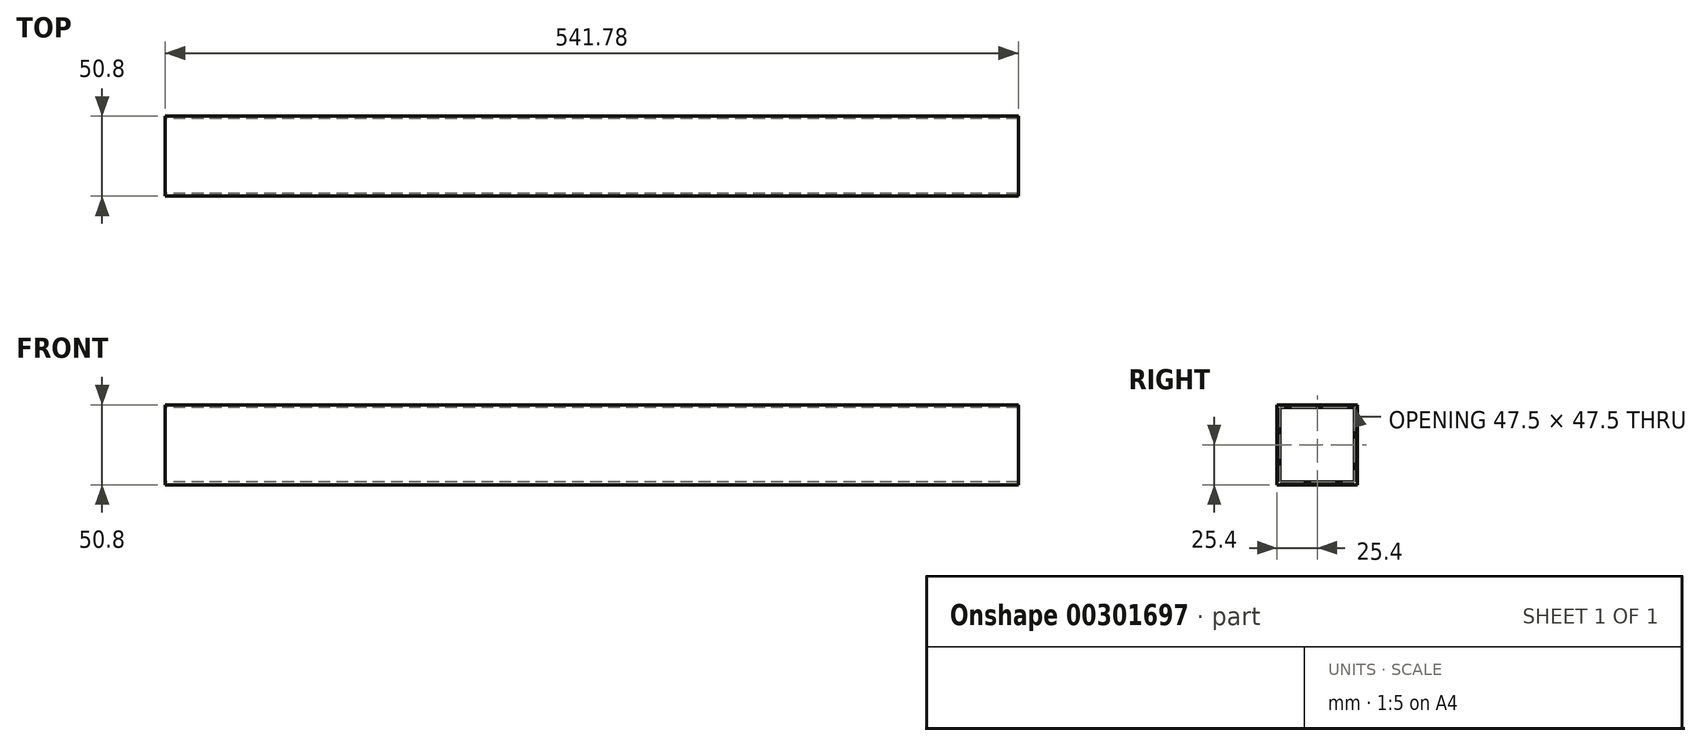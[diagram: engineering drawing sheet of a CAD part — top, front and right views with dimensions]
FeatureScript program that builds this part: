
annotation { "Feature Type Name" : "Feature", "Feature Type Description" : "" }
export const myFeature = defineFeature(function(context is Context, id is Id, definition is map)
    precondition{}
    {
        {
            var Q0;
            Q0=qCreatedBy(makeId("Right.planeOp"),FACE);
            var sketch = newSketch(context, id + "F0", { "sketchPlane" : qUnion([Q0])});
            skLineSegment(sketch, "E0.bottom", {"start": v(25.4, -25.4) * mm, "end": v(-25.4, -25.4) * mm});
            skLineSegment(sketch, "E0.top", {"start": v(25.4, 25.4) * mm, "end": v(-25.4, 25.4) * mm});
            skLineSegment(sketch, "E0.left", {"start": v(25.4, -25.4) * mm, "end": v(25.4, 25.4) * mm});
            skLineSegment(sketch, "E0.right", {"start": v(-25.4, -25.4) * mm, "end": v(-25.4, 25.4) * mm});
            skPoint(sketch, "E0.middle", {"position": v(0, 0) * mm});
            skLineSegment(sketch, "E1.0", {"start": v(22.1, 23.75) * mm, "end": v(-22.1, 23.75) * mm});
            skLineSegment(sketch, "E1.1", {"start": v(23.75, -22.1) * mm, "end": v(23.75, 22.1) * mm});
            skLineSegment(sketch, "E1.2", {"start": v(22.1, -23.75) * mm, "end": v(-22.1, -23.75) * mm});
            skLineSegment(sketch, "E1.3", {"start": v(-23.75, -22.1) * mm, "end": v(-23.75, 22.1) * mm});
            skPoint(sketch, "E2.visualSharp", {"position": v(-23.75, 23.75) * mm});
            skArc(sketch, "E2.filletArc", {"start": v(-22.1, 23.75) * mm, "mid": v(-23.27, 23.27) * mm, "end": v(-23.75, 22.1) * mm});
            skPoint(sketch, "E3.visualSharp", {"position": v(23.75, 23.75) * mm});
            skArc(sketch, "E3.filletArc", {"start": v(23.75, 22.1) * mm, "mid": v(23.27, 23.27) * mm, "end": v(22.1, 23.75) * mm});
            skPoint(sketch, "E4.visualSharp", {"position": v(23.75, -23.75) * mm});
            skArc(sketch, "E4.filletArc", {"start": v(22.1, -23.75) * mm, "mid": v(23.27, -23.27) * mm, "end": v(23.75, -22.1) * mm});
            skPoint(sketch, "E5.visualSharp", {"position": v(-23.75, -23.75) * mm});
            skArc(sketch, "E5.filletArc", {"start": v(-23.75, -22.1) * mm, "mid": v(-23.27, -23.27) * mm, "end": v(-22.1, -23.75) * mm});
            skSolve(sketch);
        }
        {
            var Q0;
            Q0=makeQuery(id+"F0.imprint","IMPRINT",FACE,{"disambiguationData":[TD([[makeQuery(id+"F0.imprint","IMPRINT",EDGE,{"derivedFrom":sQuery(id+"F0.wireOp",EDGE,"E0.bottom")}),-1.0]])]});
            extrude(context, id + "F1", {"entities" : qUnion([Q0]), "depth" : 541.78 * mm});
        }
    });
